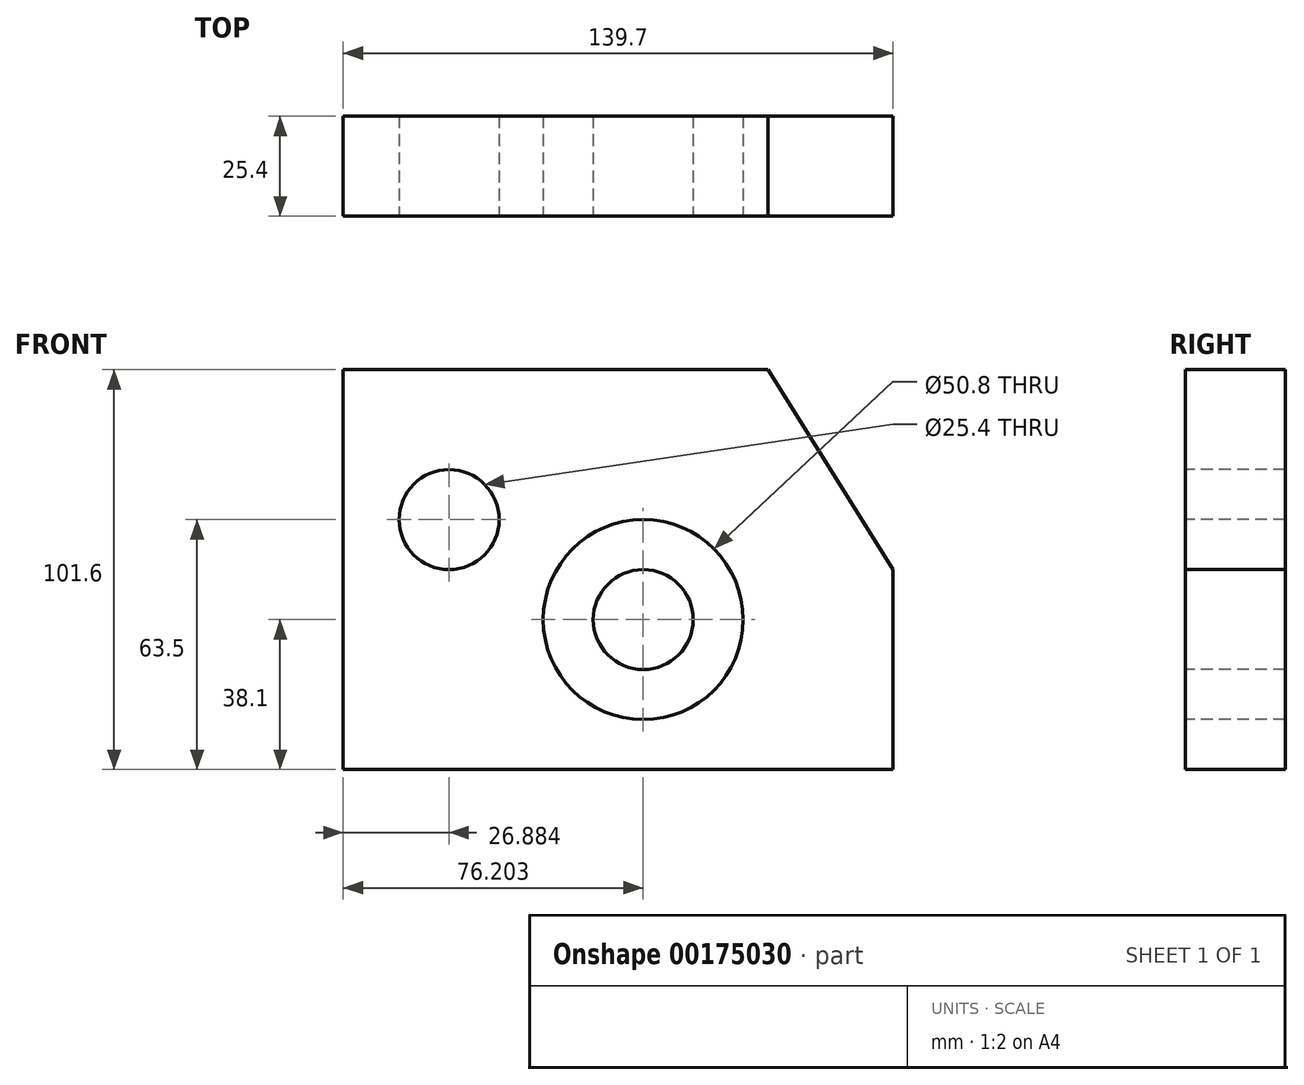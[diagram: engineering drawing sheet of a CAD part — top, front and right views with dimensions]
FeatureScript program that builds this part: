
annotation { "Feature Type Name" : "Feature", "Feature Type Description" : "" }
export const myFeature = defineFeature(function(context is Context, id is Id, definition is map)
    precondition{}
    {
        {
            var Q0;
            Q0=qCreatedBy(makeId("Front.planeOp"),FACE);
            var sketch = newSketch(context, id + "F0", { "sketchPlane" : qUnion([Q0])});
            skLineSegment(sketch, "E0", {"start": v(-57.13, 50.8) * mm, "end": v(-57.13, -50.8) * mm});
            skLineSegment(sketch, "E1", {"start": v(-57.13, 50.8) * mm, "end": v(50.82, 50.8) * mm});
            skLineSegment(sketch, "E2", {"start": v(-57.13, -50.8) * mm, "end": v(82.57, -50.8) * mm});
            skLineSegment(sketch, "E3", {"start": v(82.57, -50.8) * mm, "end": v(82.57, 0) * mm});
            skLineSegment(sketch, "E4", {"start": v(82.57, 0) * mm, "end": v(50.82, 50.8) * mm});
            skSolve(sketch);
        }
        {
            var Q0;
            Q0 = qSketchRegion(id + "F0", true);
            extrude(context, id + "F1", {"entities" : qUnion([Q0]), "depth" : 25.4 * mm});
        }
        {
            var Q0;
            Q0=makeQuery(id+"F1.opExtrude","CAP_FACE",FACE,{"disambiguationData":[OSD([sQuery(id+"F0.wireOp",EDGE,"E0"),sQuery(id+"F0.wireOp",EDGE,"E1"),sQuery(id+"F0.wireOp",EDGE,"E2"),sQuery(id+"F0.wireOp",EDGE,"E3"),sQuery(id+"F0.wireOp",EDGE,"E4")])],"isStart":false});
            var sketch = newSketch(context, id + "F2", { "sketchPlane" : qUnion([Q0])});
            skCircle(sketch, "E5", {"center": v(-30.25, 12.7) * mm, "radius": 12.7 * mm});
            skCircle(sketch, "E6", {"center": v(19.07, -12.7) * mm, "radius": 25.4 * mm});
            skCircle(sketch, "E7", {"center": v(19.07, -12.7) * mm, "radius": 12.7 * mm});
            skSolve(sketch);
        }
        {
            var Q0;
            Q0=makeQuery(id+"F2.imprint","IMPRINT",FACE,{"disambiguationData":[TD([[makeQuery(id+"F2.imprint","IMPRINT",EDGE,{"derivedFrom":sQuery(id+"F2.wireOp",EDGE,"E5")}),1.0]])]});
            var Q1;
            Q1=makeQuery(id+"F2.imprint","IMPRINT",FACE,{"disambiguationData":[TD([[makeQuery(id+"F2.imprint","IMPRINT",EDGE,{"derivedFrom":sQuery(id+"F2.wireOp",EDGE,"E6")}),1.0]])]});
            extrude(context, id + "F3", {"entities" : qUnion([Q0, Q1]), "operationType" : NewBodyOperationType.REMOVE, "oppositeDirection" : true, "depth" : 25.4 * mm});
        }
    });
